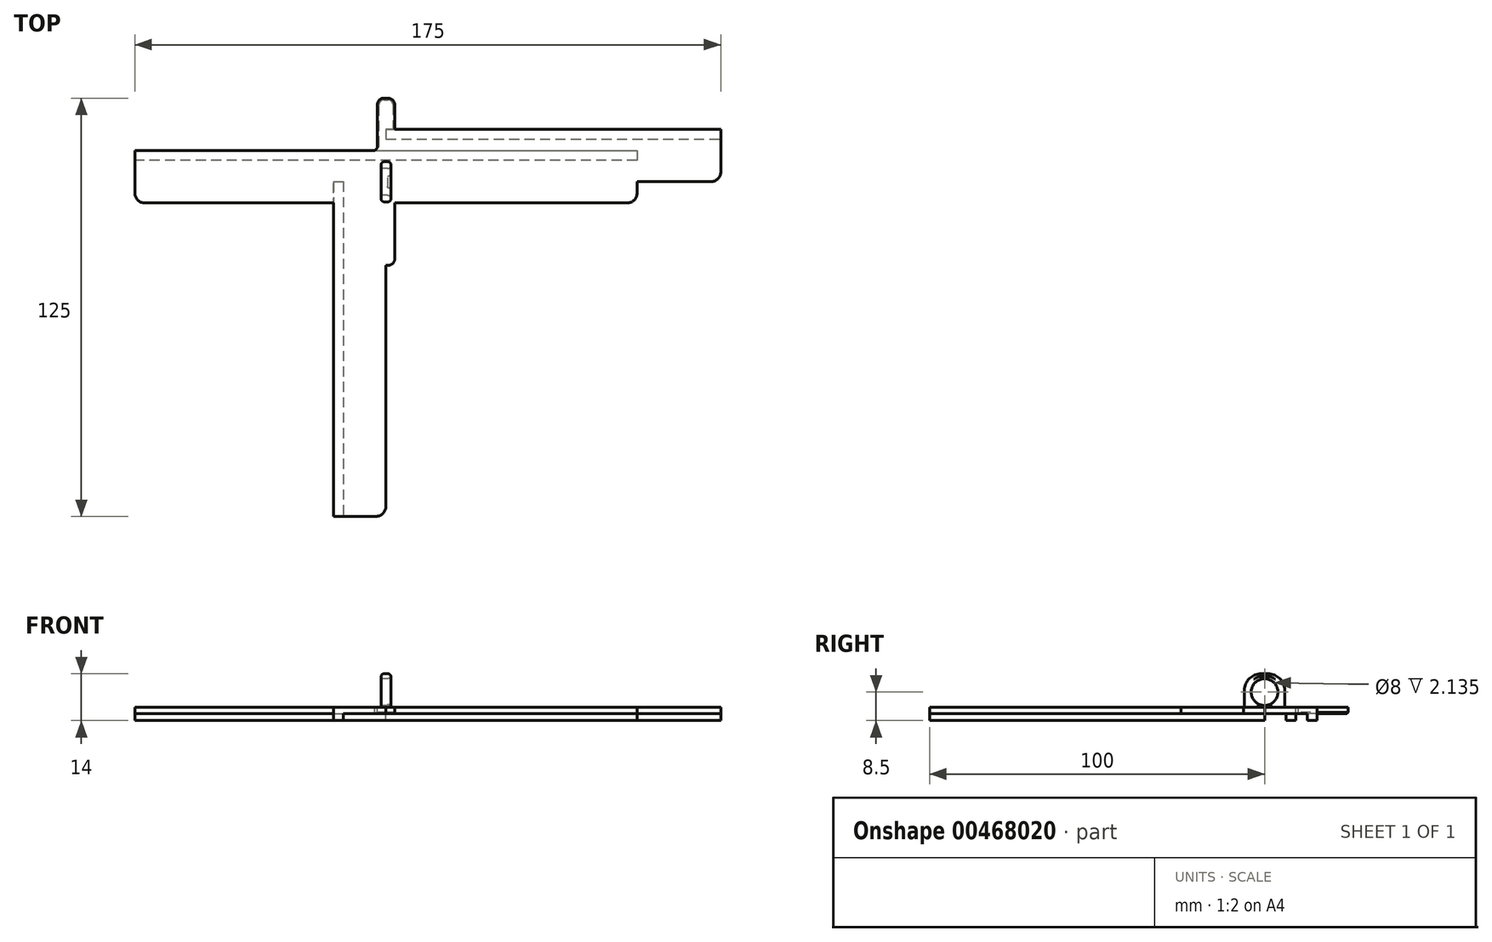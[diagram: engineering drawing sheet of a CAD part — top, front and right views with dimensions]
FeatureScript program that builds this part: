
annotation { "Feature Type Name" : "Feature", "Feature Type Description" : "" }
export const myFeature = defineFeature(function(context is Context, id is Id, definition is map)
    precondition{}
    {
        {
            var Q0;
            Q0=qCreatedBy(makeId("Top.planeOp"),FACE);
            var sketch = newSketch(context, id + "F0", { "sketchPlane" : qUnion([Q0])});
            skLineSegment(sketch, "E0.bottom", {"start": v(0, 0) * mm, "end": v(100, 0) * mm});
            skLineSegment(sketch, "E0.top", {"start": v(0, 12.7) * mm, "end": v(100, 12.7) * mm});
            skLineSegment(sketch, "E0.left", {"start": v(0, 0) * mm, "end": v(0, 12.7) * mm});
            skLineSegment(sketch, "E0.right", {"start": v(100, 0) * mm, "end": v(100, 12.7) * mm});
            skLineSegment(sketch, "E1.bottom", {"start": v(0, 0) * mm, "end": v(-12.7, 0) * mm});
            skLineSegment(sketch, "E1.top", {"start": v(0, -100) * mm, "end": v(-12.7, -100) * mm});
            skLineSegment(sketch, "E1.left", {"start": v(0, 0) * mm, "end": v(0, -100) * mm});
            skLineSegment(sketch, "E1.right", {"start": v(-12.7, 0) * mm, "end": v(-12.7, -100) * mm});
            skLineSegment(sketch, "E2", {"start": v(-12.7, 0) * mm, "end": v(0, 12.7) * mm});
            skCircle(sketch, "E3", {"center": v(0, 0) * mm, "radius": 1.5 * mm});
            skSolve(sketch);
        }
        {
            var Q0;
            {var subQ2=sQuery(id+"F0.wireOp",EDGE,"E1.top");Q0=makeQuery(id+"F0.imprint","IMPRINT",FACE,{"disambiguationData":[TD([[makeQuery(id+"F0.imprint","IMPRINT",EDGE,{"derivedFrom":subQ2}),-1.0]])]});}
            var Q1;
            {var subQ0=sQuery(id+"F0.wireOp",EDGE,"E2");Q1=makeQuery(id+"F0.imprint","IMPRINT",FACE,{"disambiguationData":[TD([[makeQuery(id+"F0.imprint","IMPRINT",EDGE,{"derivedFrom":subQ0}),-1.0]])]});}
            var Q2;
            {var subQ2=sQuery(id+"F0.wireOp",EDGE,"E0.top");Q2=makeQuery(id+"F0.imprint","IMPRINT",FACE,{"disambiguationData":[TD([[makeQuery(id+"F0.imprint","IMPRINT",EDGE,{"derivedFrom":subQ2}),-1.0]])]});}
            extrude(context, id + "F1", {"entities" : qUnion([Q0, Q1, Q2]), "depth" : 2 * mm, "offsetDistance" : 25 * mm});
        }
        {
            var Q0;
            Q0=makeQuery(id+"F1.opExtrude","SWEPT_EDGE",EDGE,{"disambiguationData":[OSD([sQuery(id+"F0.wireOp",EDGE,"E0.bottom"),sQuery(id+"F0.wireOp",EDGE,"E0.right")])]});
            var Q1;
            Q1=makeQuery(id+"F1.opExtrude","SWEPT_EDGE",EDGE,{"disambiguationData":[OSD([sQuery(id+"F0.wireOp",EDGE,"E1.top"),sQuery(id+"F0.wireOp",EDGE,"E1.left")])]});
            fillet(context, id + "F2", {"entities" : qUnion([Q0, Q1]), "radius" : 3 * mm, "tangentPropagation" : true, "allowEdgeOverflow" : false});
        }
        {
            var Q0;
            Q0=makeQuery(id+"F1.opExtrude","CAP_FACE",FACE,{"disambiguationData":[OSD([sQuery(id+"F0.wireOp",EDGE,"E0.bottom"),sQuery(id+"F0.wireOp",EDGE,"E0.top"),sQuery(id+"F0.wireOp",EDGE,"E0.right"),sQuery(id+"F0.wireOp",EDGE,"E1.top"),sQuery(id+"F0.wireOp",EDGE,"E1.left"),sQuery(id+"F0.wireOp",EDGE,"E1.right"),sQuery(id+"F0.wireOp",EDGE,"E2"),sQuery(id+"F0.wireOp",EDGE,"E3")])],"isStart":false});
            var sketch = newSketch(context, id + "F3", { "sketchPlane" : qUnion([Q0])});
            skLineSegment(sketch, "E4.bottom", {"start": v(-12.7, -100) * mm, "end": v(-15.7, -100) * mm});
            skLineSegment(sketch, "E4.top", {"start": v(-12.7, 0) * mm, "end": v(-15.7, 0) * mm});
            skLineSegment(sketch, "E4.left", {"start": v(-12.7, -100) * mm, "end": v(-12.7, 0) * mm});
            skLineSegment(sketch, "E4.right", {"start": v(-15.7, -100) * mm, "end": v(-15.7, 0) * mm});
            skLineSegment(sketch, "E5.bottom", {"start": v(0, 12.7) * mm, "end": v(100, 12.7) * mm});
            skLineSegment(sketch, "E5.top", {"start": v(0, 15.7) * mm, "end": v(100, 15.7) * mm});
            skLineSegment(sketch, "E5.left", {"start": v(0, 12.7) * mm, "end": v(0, 15.7) * mm});
            skLineSegment(sketch, "E5.right", {"start": v(100, 12.7) * mm, "end": v(100, 15.7) * mm});
            skSolve(sketch);
        }
        {
            var Q0;
            Q0=makeQuery(id+"F3.imprint","IMPRINT",FACE,{"disambiguationData":[TD([[makeQuery(id+"F3.imprint","IMPRINT",EDGE,{"derivedFrom":sQuery(id+"F3.wireOp",EDGE,"E5.bottom")}),1.0]])]});
            var Q1;
            Q1=makeQuery(id+"F3.imprint","IMPRINT",FACE,{"disambiguationData":[TD([[makeQuery(id+"F3.imprint","IMPRINT",EDGE,{"derivedFrom":sQuery(id+"F3.wireOp",EDGE,"E4.bottom")}),-1.0]])]});
            extrude(context, id + "F4", {"entities" : qUnion([Q0, Q1]), "operationType" : NewBodyOperationType.ADD, "oppositeDirection" : true, "depth" : 4 * mm, "offsetDistance" : 25 * mm});
        }
        {
            var Q0;
            Q0=makeQuery(id+"F1.opExtrude","SWEPT_EDGE",EDGE,{"disambiguationData":[OSD([sQuery(id+"F0.wireOp",EDGE,"E1.left"),sQuery(id+"F0.wireOp",EDGE,"E3")])]});
            var Q1;
            Q1=makeQuery(id+"F1.opExtrude","SWEPT_EDGE",EDGE,{"disambiguationData":[OSD([sQuery(id+"F0.wireOp",EDGE,"E0.bottom"),sQuery(id+"F0.wireOp",EDGE,"E3")])]});
            fillet(context, id + "F5", {"entities" : qUnion([Q0, Q1]), "radius" : 2 * mm, "tangentPropagation" : true, "allowEdgeOverflow" : false});
        }
        {
            var Q0;
            Q0=qCreatedBy(makeId("Top.planeOp"),FACE);
            var sketch = newSketch(context, id + "F6", { "sketchPlane" : qUnion([Q0])});
            skLineSegment(sketch, "E6.bottom", {"start": v(2.6, -25) * mm, "end": v(-2.6, -25) * mm});
            skLineSegment(sketch, "E6.top", {"start": v(2.6, 25) * mm, "end": v(-2.6, 25) * mm});
            skLineSegment(sketch, "E6.left", {"start": v(2.6, -25) * mm, "end": v(2.6, 25) * mm});
            skLineSegment(sketch, "E6.right", {"start": v(-2.6, -25) * mm, "end": v(-2.6, 25) * mm});
            skPoint(sketch, "E6.middle", {"position": v(0, 0) * mm});
            skLineSegment(sketch, "E7.bottom", {"start": v(15, 2.6) * mm, "end": v(-15, 2.6) * mm});
            skLineSegment(sketch, "E7.top", {"start": v(15, -2.6) * mm, "end": v(-15, -2.6) * mm});
            skLineSegment(sketch, "E7.left", {"start": v(15, 2.6) * mm, "end": v(15, -2.6) * mm});
            skLineSegment(sketch, "E7.right", {"start": v(-15, 2.6) * mm, "end": v(-15, -2.6) * mm});
            skCircle(sketch, "E8", {"center": v(-3.6, 3.6) * mm, "radius": 1.5 * mm});
            skCircle(sketch, "E9.MirrorC", {"center": v(3.6, 3.6) * mm, "radius": 1.5 * mm});
            skCircle(sketch, "E10.MirrorC", {"center": v(-3.6, -3.6) * mm, "radius": 1.5 * mm});
            skCircle(sketch, "E11.MirrorC", {"center": v(3.6, -3.6) * mm, "radius": 1.5 * mm});
            skSolve(sketch);
        }
        {
            var Q0;
            {var subQ6=sQuery(id+"F6.wireOp",EDGE,"E6.top");Q0=makeQuery(id+"F6.imprint","IMPRINT",FACE,{"disambiguationData":[TD([[makeQuery(id+"F6.imprint","IMPRINT",EDGE,{"derivedFrom":subQ6}),1.0]])]});}
            var Q1;
            {var subQ0=sQuery(id+"F6.wireOp",EDGE,"E11.MirrorC");var subQ13=sQuery(id+"F6.wireOp",EDGE,"E6.left");var subQ14=makeQuery(id+"F6.imprint","INTERSECT",VERTEX,{"disambiguationData":[OD(1.0)],"derivedFrom":[subQ13,subQ0]});Q1=makeQuery(id+"F6.imprint","IMPRINT",FACE,{"disambiguationData":[TD([[makeQuery(id+"F6.imprint","IMPRINT",EDGE,{"disambiguationData":[TD([[subQ14,-1.0]])],"derivedFrom":subQ13}),1.0]])]});}
            var Q2;
            {var subQ0=sQuery(id+"F6.wireOp",EDGE,"E7.left");Q2=makeQuery(id+"F6.imprint","IMPRINT",FACE,{"disambiguationData":[TD([[makeQuery(id+"F6.imprint","IMPRINT",EDGE,{"derivedFrom":subQ0}),-1.0]])]});}
            var Q3;
            {var subQ0=sQuery(id+"F6.wireOp",EDGE,"E7.right");Q3=makeQuery(id+"F6.imprint","IMPRINT",FACE,{"disambiguationData":[TD([[makeQuery(id+"F6.imprint","IMPRINT",EDGE,{"derivedFrom":subQ0}),1.0]])]});}
            var Q4;
            {var subQ6=sQuery(id+"F6.wireOp",EDGE,"E6.bottom");Q4=makeQuery(id+"F6.imprint","IMPRINT",FACE,{"disambiguationData":[TD([[makeQuery(id+"F6.imprint","IMPRINT",EDGE,{"derivedFrom":subQ6}),-1.0]])]});}
            extrude(context, id + "F7", {"entities" : qUnion([Q0, Q1, Q2, Q3, Q4]), "depth" : 2 * mm, "offsetDistance" : 25 * mm});
        }
        {
            var Q0;
            Q0=makeQuery(id+"F7.opExtrude","CAP_FACE",FACE,{"disambiguationData":[OSD([sQuery(id+"F6.wireOp",EDGE,"E6.bottom"),sQuery(id+"F6.wireOp",EDGE,"E6.top"),sQuery(id+"F6.wireOp",EDGE,"E6.left"),sQuery(id+"F6.wireOp",EDGE,"E6.right"),sQuery(id+"F6.wireOp",EDGE,"E7.bottom"),sQuery(id+"F6.wireOp",EDGE,"E7.top"),sQuery(id+"F6.wireOp",EDGE,"E7.left"),sQuery(id+"F6.wireOp",EDGE,"E7.right"),sQuery(id+"F6.wireOp",EDGE,"E8"),sQuery(id+"F6.wireOp",EDGE,"E9.MirrorC"),sQuery(id+"F6.wireOp",EDGE,"E10.MirrorC"),sQuery(id+"F6.wireOp",EDGE,"E11.MirrorC")])],"isStart":false});
            var sketch = newSketch(context, id + "F8", { "sketchPlane" : qUnion([Q0])});
            skLineSegment(sketch, "E12.bottom", {"start": v(1.5, -6) * mm, "end": v(-1.5, -6) * mm});
            skLineSegment(sketch, "E12.top", {"start": v(1.5, 6) * mm, "end": v(-1.5, 6) * mm});
            skLineSegment(sketch, "E12.left", {"start": v(1.5, -6) * mm, "end": v(1.5, 6) * mm});
            skLineSegment(sketch, "E12.right", {"start": v(-1.5, -6) * mm, "end": v(-1.5, 6) * mm});
            skPoint(sketch, "E12.middle", {"position": v(0, 0) * mm});
            skSolve(sketch);
        }
        {
            var Q0;
            Q0=makeQuery(id+"F8.imprint","IMPRINT",FACE,{"disambiguationData":[TD([[makeQuery(id+"F8.imprint","IMPRINT",EDGE,{"derivedFrom":sQuery(id+"F8.wireOp",EDGE,"E12.bottom")}),-1.0]])]});
            extrude(context, id + "F9", {"entities" : qUnion([Q0]), "operationType" : NewBodyOperationType.ADD, "depth" : 10 * mm, "offsetDistance" : 25 * mm});
        }
        {
            var Q0;
            Q0=makeQuery(id+"F7.opExtrude","SWEPT_EDGE",EDGE,{"disambiguationData":[OSD([sQuery(id+"F6.wireOp",EDGE,"E7.top"),sQuery(id+"F6.wireOp",EDGE,"E7.right")])]});
            var Q1;
            Q1=makeQuery(id+"F7.opExtrude","SWEPT_EDGE",EDGE,{"disambiguationData":[OSD([sQuery(id+"F6.wireOp",EDGE,"E7.bottom"),sQuery(id+"F6.wireOp",EDGE,"E7.right")])]});
            var Q2;
            Q2=makeQuery(id+"F7.opExtrude","SWEPT_EDGE",EDGE,{"disambiguationData":[OSD([sQuery(id+"F6.wireOp",EDGE,"E6.top"),sQuery(id+"F6.wireOp",EDGE,"E6.right")])]});
            var Q3;
            Q3=makeQuery(id+"F7.opExtrude","SWEPT_EDGE",EDGE,{"disambiguationData":[OSD([sQuery(id+"F6.wireOp",EDGE,"E6.bottom"),sQuery(id+"F6.wireOp",EDGE,"E6.right")])]});
            var Q4;
            Q4=makeQuery(id+"F7.opExtrude","SWEPT_EDGE",EDGE,{"disambiguationData":[OSD([sQuery(id+"F6.wireOp",EDGE,"E6.bottom"),sQuery(id+"F6.wireOp",EDGE,"E6.left")])]});
            var Q5;
            Q5=makeQuery(id+"F7.opExtrude","SWEPT_EDGE",EDGE,{"disambiguationData":[OSD([sQuery(id+"F6.wireOp",EDGE,"E7.top"),sQuery(id+"F6.wireOp",EDGE,"E7.left")])]});
            var Q6;
            Q6=makeQuery(id+"F7.opExtrude","SWEPT_EDGE",EDGE,{"disambiguationData":[OSD([sQuery(id+"F6.wireOp",EDGE,"E6.top"),sQuery(id+"F6.wireOp",EDGE,"E6.left")])]});
            var Q7;
            Q7=makeQuery(id+"F7.opExtrude","SWEPT_EDGE",EDGE,{"disambiguationData":[OSD([sQuery(id+"F6.wireOp",EDGE,"E7.bottom"),sQuery(id+"F6.wireOp",EDGE,"E7.left")])]});
            fillet(context, id + "F10", {"entities" : qUnion([Q0, Q1, Q2, Q3, Q4, Q5, Q6, Q7]), "radius" : 2 * mm, "tangentPropagation" : true, "allowEdgeOverflow" : false});
        }
        {
            var Q0;
            {var subQ0=sQuery(id+"F6.wireOp",EDGE,"E7.top");Q0=makeQuery(id+"F7.opExtrude","CAP_EDGE",EDGE,{"disambiguationData":[OSD([subQ0]),TDD([makeQuery(id+"F6.imprint","IMPRINT",EDGE,{"disambiguationData":[TD([[makeQuery(id+"F6.imprint","INTERSECT",VERTEX,{"derivedFrom":[subQ0,sQuery(id+"F6.wireOp",EDGE,"E7.right")]}),1.0]])],"derivedFrom":subQ0})])],"isStart":true});}
            var Q1;
            {var subQ0=sQuery(id+"F6.wireOp",EDGE,"E6.right");Q1=makeQuery(id+"F7.opExtrude","CAP_EDGE",EDGE,{"disambiguationData":[OSD([subQ0]),TDD([makeQuery(id+"F6.imprint","IMPRINT",EDGE,{"disambiguationData":[TD([[makeQuery(id+"F6.imprint","INTERSECT",VERTEX,{"derivedFrom":[sQuery(id+"F6.wireOp",EDGE,"E6.bottom"),subQ0]}),-1.0]])],"derivedFrom":subQ0})])],"isStart":true});}
            var Q2;
            {var subQ0=sQuery(id+"F6.wireOp",EDGE,"E7.top");Q2=makeQuery(id+"F7.opExtrude","CAP_EDGE",EDGE,{"disambiguationData":[OSD([subQ0]),TDD([makeQuery(id+"F6.imprint","IMPRINT",EDGE,{"disambiguationData":[TD([[makeQuery(id+"F6.imprint","INTERSECT",VERTEX,{"derivedFrom":[subQ0,sQuery(id+"F6.wireOp",EDGE,"E7.left")]}),-1.0]])],"derivedFrom":subQ0})])],"isStart":true});}
            var Q3;
            {var subQ0=sQuery(id+"F6.wireOp",EDGE,"E6.right");Q3=makeQuery(id+"F7.opExtrude","CAP_EDGE",EDGE,{"disambiguationData":[OSD([subQ0]),TDD([makeQuery(id+"F6.imprint","IMPRINT",EDGE,{"disambiguationData":[TD([[makeQuery(id+"F6.imprint","INTERSECT",VERTEX,{"derivedFrom":[sQuery(id+"F6.wireOp",EDGE,"E6.top"),subQ0]}),1.0]])],"derivedFrom":subQ0})])],"isStart":true});}
            chamfer(context, id + "F11", {"entities" : qUnion([Q0, Q1, Q2, Q3]), "width" : 0.5 * mm, "tangentPropagation" : true});
        }
        {
            var Q0;
            Q0=makeQuery(id+"F9.opExtrude","CAP_EDGE",EDGE,{"disambiguationData":[OSD([sQuery(id+"F8.wireOp",EDGE,"E12.top")])],"isStart":false});
            var Q1;
            Q1=makeQuery(id+"F9.opExtrude","CAP_EDGE",EDGE,{"disambiguationData":[OSD([sQuery(id+"F8.wireOp",EDGE,"E12.bottom")])],"isStart":false});
            fillet(context, id + "F12", {"entities" : qUnion([Q0, Q1]), "radius" : 5 * mm, "tangentPropagation" : true, "allowEdgeOverflow" : false});
        }
        {
            var Q0;
            Q0=makeQuery(id+"F9.opExtrude","SWEPT_FACE",FACE,{"disambiguationData":[OSD([sQuery(id+"F8.wireOp",EDGE,"E12.right")])]});
            var sketch = newSketch(context, id + "F13", { "sketchPlane" : qUnion([Q0])});
            skCircle(sketch, "E13", {"center": v(0, 6.5) * mm, "radius": 4 * mm});
            skSolve(sketch);
        }
        {
            var Q0;
            Q0=makeQuery(id+"F13.imprint","IMPRINT",FACE,{"disambiguationData":[TD([[makeQuery(id+"F13.imprint","IMPRINT",EDGE,{"derivedFrom":sQuery(id+"F13.wireOp",EDGE,"E13")}),1.0]])]});
            extrude(context, id + "F14", {"entities" : qUnion([Q0]), "operationType" : NewBodyOperationType.REMOVE, "oppositeDirection" : true, "depth" : 25 * mm, "offsetDistance" : 25 * mm});
        }
        {
            var Q0;
            Q0=makeQuery(id+"F9.opExtrude","SWEPT_EDGE",EDGE,{"disambiguationData":[OSD([sQuery(id+"F8.wireOp",EDGE,"E12.top"),sQuery(id+"F8.wireOp",EDGE,"E12.right")])]});
            var Q1;
            Q1=makeQuery(id+"F14.boolean.opBoolean","COPY",EDGE,{"derivedFrom":makeQuery(id+"F14.opExtrude","CAP_EDGE",EDGE,{"disambiguationData":[OSD([sQuery(id+"F13.wireOp",EDGE,"E13")])],"isStart":true})});
            var Q2;
            Q2=makeQuery(id+"F14.boolean.opBoolean","INTERSECT",EDGE,{"derivedFrom":[makeQuery(id+"F9.opExtrude","SWEPT_FACE",FACE,{"disambiguationData":[OSD([sQuery(id+"F8.wireOp",EDGE,"E12.left")])]}),makeQuery(id+"F14.opExtrude","SWEPT_FACE",FACE,{"disambiguationData":[OSD([sQuery(id+"F13.wireOp",EDGE,"E13")])]})]});
            var Q3;
            Q3=makeQuery(id+"F12.opFillet","BLEND_EDGE",EDGE,{"blendedFrom":[makeQuery(id+"F9.opExtrude","CAP_EDGE",EDGE,{"disambiguationData":[OSD([sQuery(id+"F8.wireOp",EDGE,"E12.bottom")])],"isStart":false}),makeQuery(id+"F9.opExtrude","SWEPT_FACE",FACE,{"disambiguationData":[OSD([sQuery(id+"F8.wireOp",EDGE,"E12.left")])]})],"blendedInto":[makeQuery(id+"F9.opExtrude","SWEPT_FACE",FACE,{"disambiguationData":[OSD([sQuery(id+"F8.wireOp",EDGE,"E12.left")])]})]});
            fillet(context, id + "F15", {"entities" : qUnion([Q0, Q1, Q2, Q3]), "radius" : 1 * mm, "tangentPropagation" : true, "allowEdgeOverflow" : false});
        }
        {
            var Q0;
            Q0=qCreatedBy(makeId("Top.planeOp"),FACE);
            var sketch = newSketch(context, id + "F16", { "sketchPlane" : qUnion([Q0])});
            skLineSegment(sketch, "E14.bottom", {"start": v(75, -6.35) * mm, "end": v(-75, -6.35) * mm});
            skLineSegment(sketch, "E14.top", {"start": v(75, 6.35) * mm, "end": v(-75, 6.35) * mm});
            skLineSegment(sketch, "E14.left", {"start": v(75, -6.35) * mm, "end": v(75, 6.35) * mm});
            skLineSegment(sketch, "E14.right", {"start": v(-75, -6.35) * mm, "end": v(-75, 6.35) * mm});
            skPoint(sketch, "E14.middle", {"position": v(0, 0) * mm});
            skSolve(sketch);
        }
        {
            var Q0;
            Q0=makeQuery(id+"F16.imprint","IMPRINT",FACE,{"disambiguationData":[TD([[makeQuery(id+"F16.imprint","IMPRINT",EDGE,{"derivedFrom":sQuery(id+"F16.wireOp",EDGE,"E14.bottom")}),-1.0]])]});
            extrude(context, id + "F17", {"entities" : qUnion([Q0]), "depth" : 2 * mm, "offsetDistance" : 25 * mm});
        }
        {
            var Q0;
            Q0=makeQuery(id+"F17.opExtrude","SWEPT_EDGE",EDGE,{"disambiguationData":[OSD([sQuery(id+"F16.wireOp",EDGE,"E14.bottom"),sQuery(id+"F16.wireOp",EDGE,"E14.right")])]});
            var Q1;
            Q1=makeQuery(id+"F17.opExtrude","SWEPT_EDGE",EDGE,{"disambiguationData":[OSD([sQuery(id+"F16.wireOp",EDGE,"E14.bottom"),sQuery(id+"F16.wireOp",EDGE,"E14.left")])]});
            fillet(context, id + "F18", {"entities" : qUnion([Q0, Q1]), "radius" : 3 * mm, "tangentPropagation" : true, "allowEdgeOverflow" : false});
        }
        {
            var Q0;
            Q0=makeQuery(id+"F17.opExtrude","CAP_FACE",FACE,{"disambiguationData":[OSD([sQuery(id+"F16.wireOp",EDGE,"E14.bottom"),sQuery(id+"F16.wireOp",EDGE,"E14.top"),sQuery(id+"F16.wireOp",EDGE,"E14.left"),sQuery(id+"F16.wireOp",EDGE,"E14.right")])],"isStart":false});
            var sketch = newSketch(context, id + "F19", { "sketchPlane" : qUnion([Q0])});
            skLineSegment(sketch, "E15.bottom", {"start": v(-75, 6.35) * mm, "end": v(75, 6.35) * mm});
            skLineSegment(sketch, "E15.top", {"start": v(-75, 9.35) * mm, "end": v(75, 9.35) * mm});
            skLineSegment(sketch, "E15.left", {"start": v(-75, 6.35) * mm, "end": v(-75, 9.35) * mm});
            skLineSegment(sketch, "E15.right", {"start": v(75, 6.35) * mm, "end": v(75, 9.35) * mm});
            skSolve(sketch);
        }
        {
            var Q0;
            Q0=makeQuery(id+"F19.imprint","IMPRINT",FACE,{"disambiguationData":[TD([[makeQuery(id+"F19.imprint","IMPRINT",EDGE,{"derivedFrom":sQuery(id+"F19.wireOp",EDGE,"E15.bottom")}),-1.0]])]});
            extrude(context, id + "F20", {"entities" : qUnion([Q0]), "operationType" : NewBodyOperationType.ADD, "oppositeDirection" : true, "depth" : 4 * mm, "offsetDistance" : 25 * mm});
        }
    });
